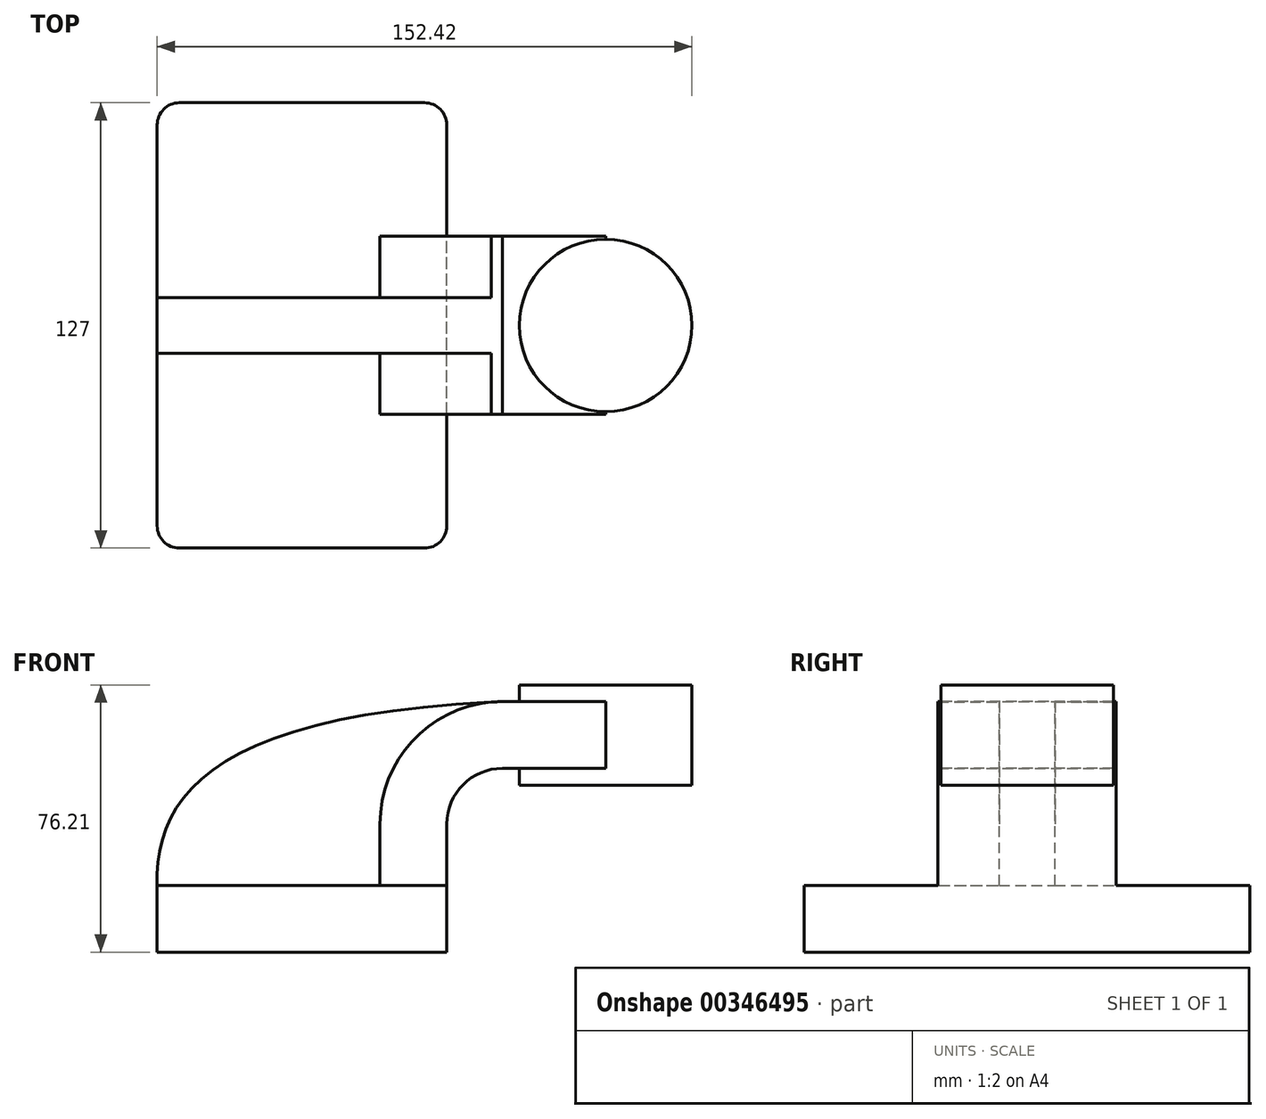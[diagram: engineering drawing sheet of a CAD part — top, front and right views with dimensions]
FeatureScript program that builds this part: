
annotation { "Feature Type Name" : "Feature", "Feature Type Description" : "" }
export const myFeature = defineFeature(function(context is Context, id is Id, definition is map)
    precondition{}
    {
        {
            var Q0;
            Q0=qCreatedBy(makeId("Front.planeOp"),FACE);
            var sketch = newSketch(context, id + "F0", { "sketchPlane" : qUnion([Q0])});
            skLineSegment(sketch, "E0.bottom", {"start": v(-41.28, 9.52) * mm, "end": v(41.28, 9.53) * mm});
            skLineSegment(sketch, "E0.top", {"start": v(-41.28, -9.53) * mm, "end": v(41.28, -9.53) * mm});
            skLineSegment(sketch, "E0.left", {"start": v(-41.28, 9.52) * mm, "end": v(-41.28, -9.53) * mm});
            skLineSegment(sketch, "E0.right", {"start": v(41.28, 9.53) * mm, "end": v(41.28, -9.52) * mm});
            skPoint(sketch, "E0.middle", {"position": v(0, 0) * mm});
            skLineSegment(sketch, "E1.bottom", {"start": v(111.12, 66.68) * mm, "end": v(60.32, 66.68) * mm});
            skLineSegment(sketch, "E1.top", {"start": v(111.12, 38.1) * mm, "end": v(60.32, 38.1) * mm});
            skLineSegment(sketch, "E1.left", {"start": v(111.12, 66.68) * mm, "end": v(111.12, 38.1) * mm});
            skLineSegment(sketch, "E1.right", {"start": v(60.32, 66.67) * mm, "end": v(60.32, 38.1) * mm});
            skPoint(sketch, "E1.middle", {"position": v(85.72, 52.39) * mm});
            skLineSegment(sketch, "E2", {"start": v(41.27, 9.53) * mm, "end": v(41.27, 27) * mm});
            skArc(sketch, "E3", {"start": v(41.27, 27) * mm, "mid": v(45.92, 38.23) * mm, "end": v(57.15, 42.88) * mm});
            skLineSegment(sketch, "E4", {"start": v(57.15, 42.88) * mm, "end": v(86.54, 42.88) * mm});
            skLineSegment(sketch, "E5.0", {"start": v(57.15, 61.93) * mm, "end": v(86.54, 61.93) * mm});
            skArc(sketch, "E5.1", {"start": v(22.22, 27) * mm, "mid": v(32.45, 51.7) * mm, "end": v(57.15, 61.93) * mm});
            skLineSegment(sketch, "E5.2", {"start": v(22.22, 9.53) * mm, "end": v(22.22, 27) * mm});
            skPoint(sketch, "E6.startSnap0", {"position": v(85.72, 38.1) * mm});
            skFitSpline(sketch, "E7", {"points": [v(-41.28, 9.52) * mm, v(57.15, 61.93) * mm], "startDerivative": vector(-1.9, 77.08) * mm, "endDerivative": vector(246.35, 10.57) * mm});
            skLineSegment(sketch, "E8", {"start": v(86.54, 66.68) * mm, "end": v(86.54, 38.1) * mm});
            skSolve(sketch);
        }
        {
            var Q0;
            Q0=makeQuery(id+"F0.imprint","IMPRINT",FACE,{"disambiguationData":[TD([[makeQuery(id+"F0.imprint","IMPRINT",EDGE,{"derivedFrom":sQuery(id+"F0.wireOp",EDGE,"E0.top")}),1.0]])]});
            extrude(context, id + "F1", {"entities" : qUnion([Q0]), "depth" : 127 * mm, "symmetric" : true});
        }
        {
            var Q0;
            {var subQ1=sQuery(id+"F0.wireOp",EDGE,"E2");Q0=makeQuery(id+"F0.imprint","IMPRINT",FACE,{"disambiguationData":[TD([[makeQuery(id+"F0.imprint","IMPRINT",EDGE,{"derivedFrom":subQ1}),1.0]])]});}
            var Q1;
            {var subQ0=sQuery(id+"F0.wireOp",EDGE,"E5.0");var subQ1=sQuery(id+"F0.wireOp",EDGE,"E1.right");var subQ2=makeQuery(id+"F0.imprint","INTERSECT",VERTEX,{"derivedFrom":[subQ1,subQ0]});Q1=makeQuery(id+"F0.imprint","IMPRINT",FACE,{"disambiguationData":[TD([[makeQuery(id+"F0.imprint","IMPRINT",EDGE,{"disambiguationData":[TD([[subQ2,-1.0]])],"derivedFrom":subQ1}),1.0]])]});}
            extrude(context, id + "F2", {"entities" : qUnion([Q0, Q1]), "operationType" : NewBodyOperationType.ADD, "depth" : 50.8 * mm, "symmetric" : true});
        }
        {
            var Q0;
            {var subQ3=sQuery(id+"F0.wireOp",EDGE,"E5.2");Q0=makeQuery(id+"F0.imprint","IMPRINT",FACE,{"disambiguationData":[TD([[makeQuery(id+"F0.imprint","IMPRINT",EDGE,{"derivedFrom":subQ3}),1.0]])]});}
            extrude(context, id + "F3", {"entities" : qUnion([Q0]), "operationType" : NewBodyOperationType.ADD, "depth" : 15.88 * mm, "symmetric" : true});
        }
        {
            var Q0;
            {var subQ4=sQuery(id+"F0.wireOp",EDGE,"E1.left");Q0=makeQuery(id+"F0.imprint","IMPRINT",FACE,{"disambiguationData":[TD([[makeQuery(id+"F0.imprint","IMPRINT",EDGE,{"derivedFrom":subQ4}),-1.0]])]});}
            var Q1;
            Q1=sQuery(id+"F0.wireOp",EDGE,"E8");
            revolve(context, id + "F4", {"operationType" : NewBodyOperationType.ADD, "entities" : qUnion([Q0]), "axis" : qUnion([Q1]), "revolveType" : RevolveType.FULL});
        }
        {
            var Q0;
            Q0=makeQuery(id+"F1.opExtrude","CAP_EDGE",EDGE,{"disambiguationData":[OSD([sQuery(id+"F0.wireOp",EDGE,"E0.right")])],"isStart":false});
            var Q1;
            Q1=makeQuery(id+"F1.opExtrude","CAP_EDGE",EDGE,{"disambiguationData":[OSD([sQuery(id+"F0.wireOp",EDGE,"E0.right")])],"isStart":true});
            var Q2;
            Q2=makeQuery(id+"F1.opExtrude","CAP_EDGE",EDGE,{"disambiguationData":[OSD([sQuery(id+"F0.wireOp",EDGE,"E0.left")])],"isStart":true});
            var Q3;
            Q3=makeQuery(id+"F1.opExtrude","CAP_EDGE",EDGE,{"disambiguationData":[OSD([sQuery(id+"F0.wireOp",EDGE,"E0.left")])],"isStart":false});
            fillet(context, id + "F5", {"entities" : qUnion([Q0, Q1, Q2, Q3]), "radius" : 6.35 * mm, "tangentPropagation" : true, "allowEdgeOverflow" : false});
        }
    });
